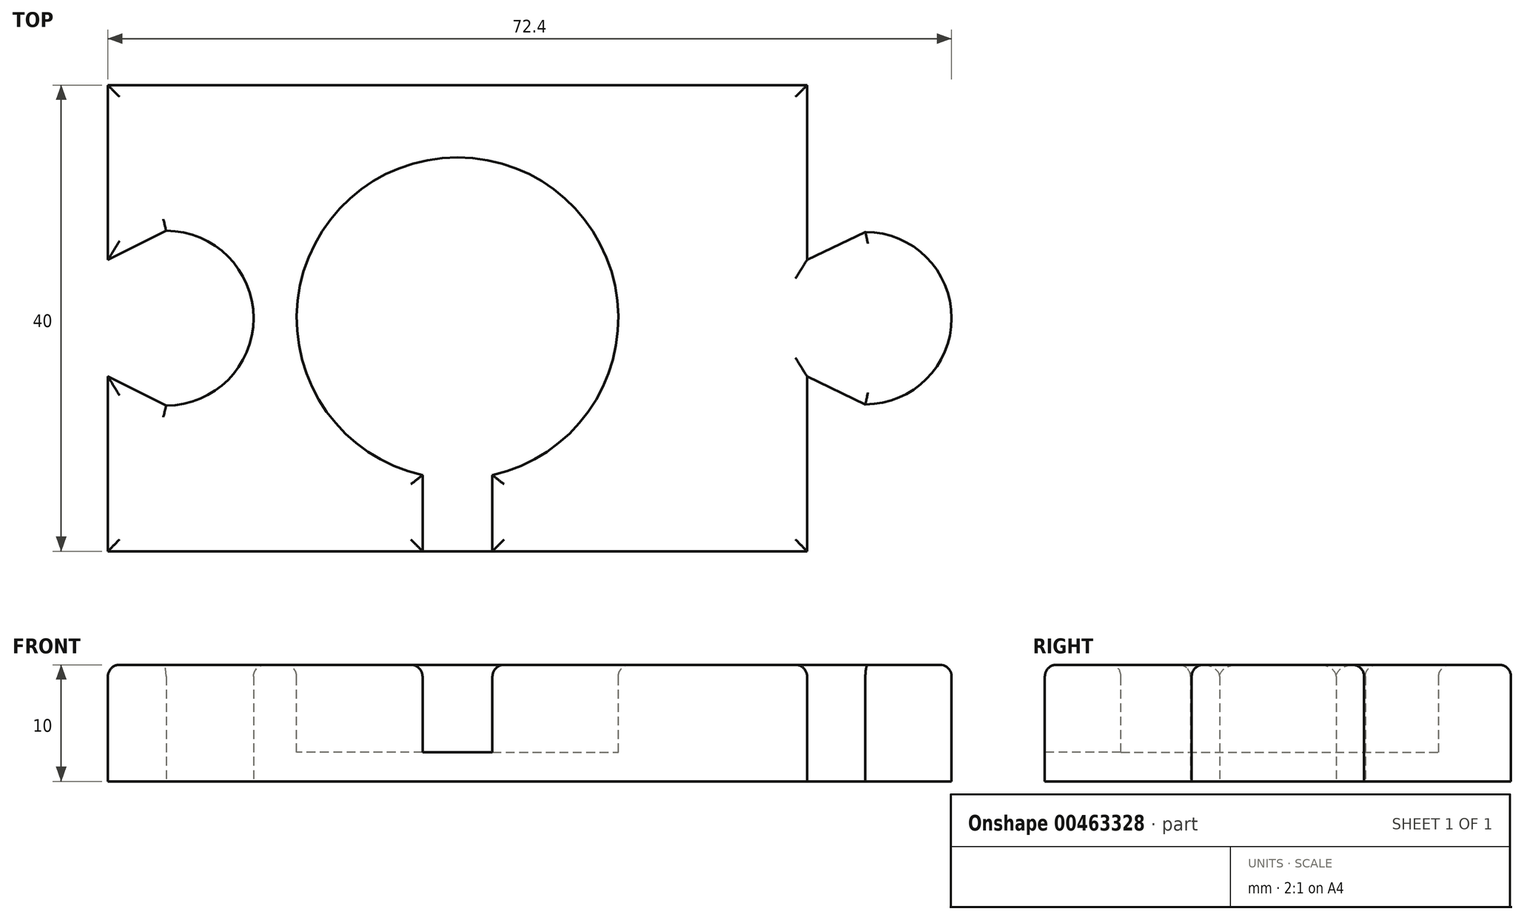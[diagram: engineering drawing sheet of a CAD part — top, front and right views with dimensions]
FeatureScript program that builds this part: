
annotation { "Feature Type Name" : "Feature", "Feature Type Description" : "" }
export const myFeature = defineFeature(function(context is Context, id is Id, definition is map)
    precondition{}
    {
        {
            var Q0;
            Q0=qCreatedBy(makeId("Top.planeOp"),FACE);
            var sketch = newSketch(context, id + "F0", { "sketchPlane" : qUnion([Q0])});
            skLineSegment(sketch, "E0.bottom", {"start": v(0, 0) * mm, "end": v(60, 0) * mm});
            skLineSegment(sketch, "E0.top", {"start": v(0, 40) * mm, "end": v(60, 40) * mm});
            skLineSegment(sketch, "E0.left", {"start": v(0, 0) * mm, "end": v(0, 15) * mm});
            skLineSegment(sketch, "E0.right", {"start": v(60, 0) * mm, "end": v(60, 15) * mm});
            skLineSegment(sketch, "E1", {"start": v(5, 12.5) * mm, "end": v(0, 15) * mm});
            skLineSegment(sketch, "E2", {"start": v(0, 25) * mm, "end": v(5, 27.5) * mm});
            skArc(sketch, "E3.trimOffspring", {"start": v(5, 12.5) * mm, "mid": v(12.5, 20) * mm, "end": v(5, 27.5) * mm});
            skLineSegment(sketch, "E4.trimOffspring", {"start": v(0, 25) * mm, "end": v(0, 40) * mm});
            skPoint(sketch, "E5.orphan", {"position": v(0, 20) * mm});
            skLineSegment(sketch, "E6", {"start": v(60, 40) * mm, "end": v(60, 25) * mm});
            skLineSegment(sketch, "E7", {"start": v(65, 27.4) * mm, "end": v(60, 25) * mm});
            skLineSegment(sketch, "E8", {"start": v(65, 12.6) * mm, "end": v(60, 15) * mm});
            skArc(sketch, "E9", {"start": v(65, 12.6) * mm, "mid": v(72.4, 20) * mm, "end": v(65, 27.4) * mm});
            skLineSegment(sketch, "E10.trimOffspring", {"start": v(60, 25) * mm, "end": v(60, 40) * mm});
            skPoint(sketch, "E11.orphan", {"position": v(60, 20) * mm});
            skSolve(sketch);
        }
        {
            var Q0;
            Q0=makeQuery(id+"F0.imprint","IMPRINT",FACE,{"disambiguationData":[TD([[makeQuery(id+"F0.imprint","IMPRINT",EDGE,{"derivedFrom":sQuery(id+"F0.wireOp",EDGE,"E0.bottom")}),1.0]])]});
            extrude(context, id + "F1", {"entities" : qUnion([Q0]), "depth" : 10 * mm});
        }
        {
            var Q0;
            Q0=makeQuery(id+"F1.opExtrude","CAP_FACE",FACE,{"disambiguationData":[OSD([sQuery(id+"F0.wireOp",EDGE,"E0.bottom"),sQuery(id+"F0.wireOp",EDGE,"E0.top"),sQuery(id+"F0.wireOp",EDGE,"E0.right"),sQuery(id+"F0.wireOp",EDGE,"E0.left"),sQuery(id+"F0.wireOp",EDGE,"E1"),sQuery(id+"F0.wireOp",EDGE,"E2"),sQuery(id+"F0.wireOp",EDGE,"E3.trimOffspring"),sQuery(id+"F0.wireOp",EDGE,"E4.trimOffspring"),sQuery(id+"F0.wireOp",EDGE,"E7"),sQuery(id+"F0.wireOp",EDGE,"E8"),sQuery(id+"F0.wireOp",EDGE,"E9"),sQuery(id+"F0.wireOp",EDGE,"E10.trimOffspring")])],"isStart":false});
            var sketch = newSketch(context, id + "F2", { "sketchPlane" : qUnion([Q0])});
            skLineSegment(sketch, "E12", {"start": v(60, 40) * mm, "end": v(41.48, 27.65) * mm});
            skLineSegment(sketch, "E13", {"start": v(0, 40) * mm, "end": v(18.52, 27.65) * mm});
            skArc(sketch, "E14", {"start": v(33, 6.53) * mm, "mid": v(30, 33.8) * mm, "end": v(27, 6.53) * mm});
            skLineSegment(sketch, "E15", {"start": v(27, 6.53) * mm, "end": v(27, 0) * mm});
            skLineSegment(sketch, "E16.trimOffspring", {"start": v(41.48, 12.35) * mm, "end": v(60, 0) * mm});
            skLineSegment(sketch, "E17.trimOffspring", {"start": v(18.52, 12.35) * mm, "end": v(0, 0) * mm});
            skLineSegment(sketch, "E18.trimOffspring", {"start": v(33, 6.53) * mm, "end": v(33, 0) * mm});
            skSolve(sketch);
        }
        {
            var Q0;
            {var subQ6=sQuery(id+"F2.wireOp",EDGE,"E15");Q0=makeQuery(id+"F2.imprint","IMPRINT",FACE,{"disambiguationData":[TD([[makeQuery(id+"F2.imprint","IMPRINT",EDGE,{"derivedFrom":subQ6}),1.0]])]});}
            extrude(context, id + "F3", {"entities" : qUnion([Q0]), "operationType" : NewBodyOperationType.REMOVE, "oppositeDirection" : true, "depth" : 7.5 * mm});
        }
        {
            var Q0;
            Q0=makeQuery(id+"F1.opExtrude","CAP_FACE",FACE,{"disambiguationData":[OSD([sQuery(id+"F0.wireOp",EDGE,"E0.bottom"),sQuery(id+"F0.wireOp",EDGE,"E0.top"),sQuery(id+"F0.wireOp",EDGE,"E0.right"),sQuery(id+"F0.wireOp",EDGE,"E0.left"),sQuery(id+"F0.wireOp",EDGE,"E1"),sQuery(id+"F0.wireOp",EDGE,"E2"),sQuery(id+"F0.wireOp",EDGE,"E3.trimOffspring"),sQuery(id+"F0.wireOp",EDGE,"E4.trimOffspring"),sQuery(id+"F0.wireOp",EDGE,"E7"),sQuery(id+"F0.wireOp",EDGE,"E8"),sQuery(id+"F0.wireOp",EDGE,"E9"),sQuery(id+"F0.wireOp",EDGE,"E10.trimOffspring")])],"isStart":false});
            fillet(context, id + "F4", {"entities" : qUnion([Q0]), "radius" : 1 * mm, "tangentPropagation" : true, "allowEdgeOverflow" : false});
        }
    });
